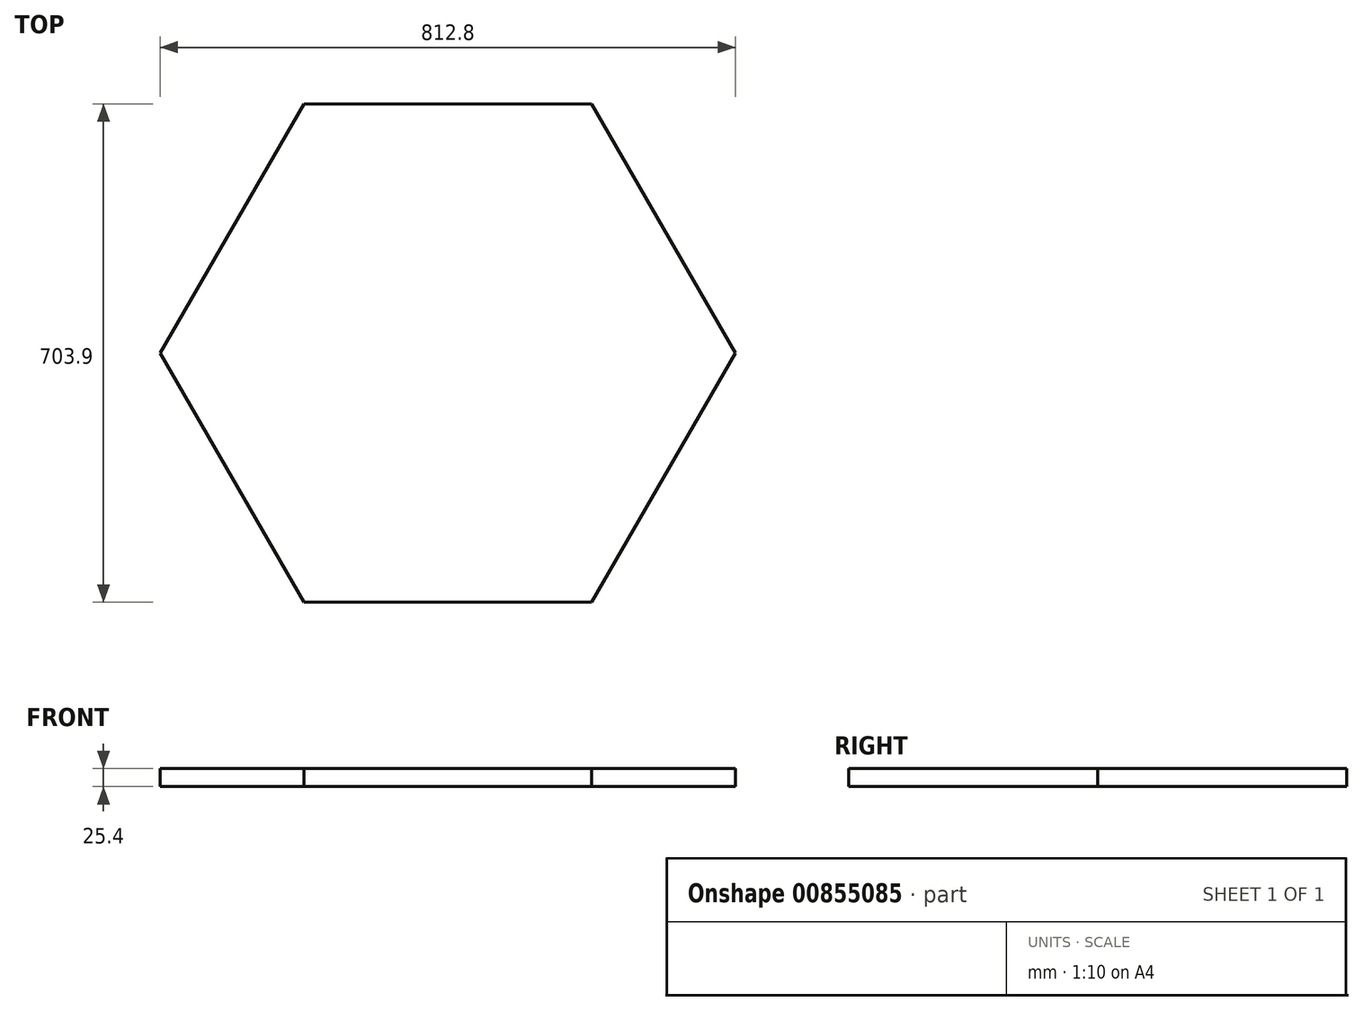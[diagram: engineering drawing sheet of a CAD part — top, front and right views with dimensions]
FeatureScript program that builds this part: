
annotation { "Feature Type Name" : "Feature", "Feature Type Description" : "" }
export const myFeature = defineFeature(function(context is Context, id is Id, definition is map)
    precondition{}
    {
        {
            var Q0;
            Q0=qCreatedBy(makeId("Top.planeOp"),FACE);
            var sketch = newSketch(context, id + "F0", { "sketchPlane" : qUnion([Q0])});
            skCircle(sketch, "E0.cCircle", {"center": v(0, 0) * mm, "radius": 406.4 * mm, "construction": true});
            skLineSegment(sketch, "E0.0", {"start": v(203.2, 351.95) * mm, "end": v(406.4, 0) * mm});
            skLineSegment(sketch, "E0.1", {"start": v(406.4, 0) * mm, "end": v(203.2, -351.95) * mm});
            skLineSegment(sketch, "E0.2", {"start": v(203.2, -351.95) * mm, "end": v(-203.2, -351.95) * mm});
            skLineSegment(sketch, "E0.3", {"start": v(-203.2, -351.95) * mm, "end": v(-406.4, 0) * mm});
            skLineSegment(sketch, "E0.4", {"start": v(-406.4, 0) * mm, "end": v(-203.2, 351.95) * mm});
            skLineSegment(sketch, "E0.5", {"start": v(-203.2, 351.95) * mm, "end": v(203.2, 351.95) * mm});
            skSolve(sketch);
        }
        {
            var Q0;
            Q0=makeQuery(id+"F0.imprint","IMPRINT",FACE,{"disambiguationData":[TD([[makeQuery(id+"F0.imprint","IMPRINT",EDGE,{"derivedFrom":sQuery(id+"F0.wireOp",EDGE,"E0.0")}),-1.0]])]});
            extrude(context, id + "F1", {"entities" : qUnion([Q0]), "depth" : 25.4 * mm, "offsetDistance" : 25.4 * mm});
        }
    });
